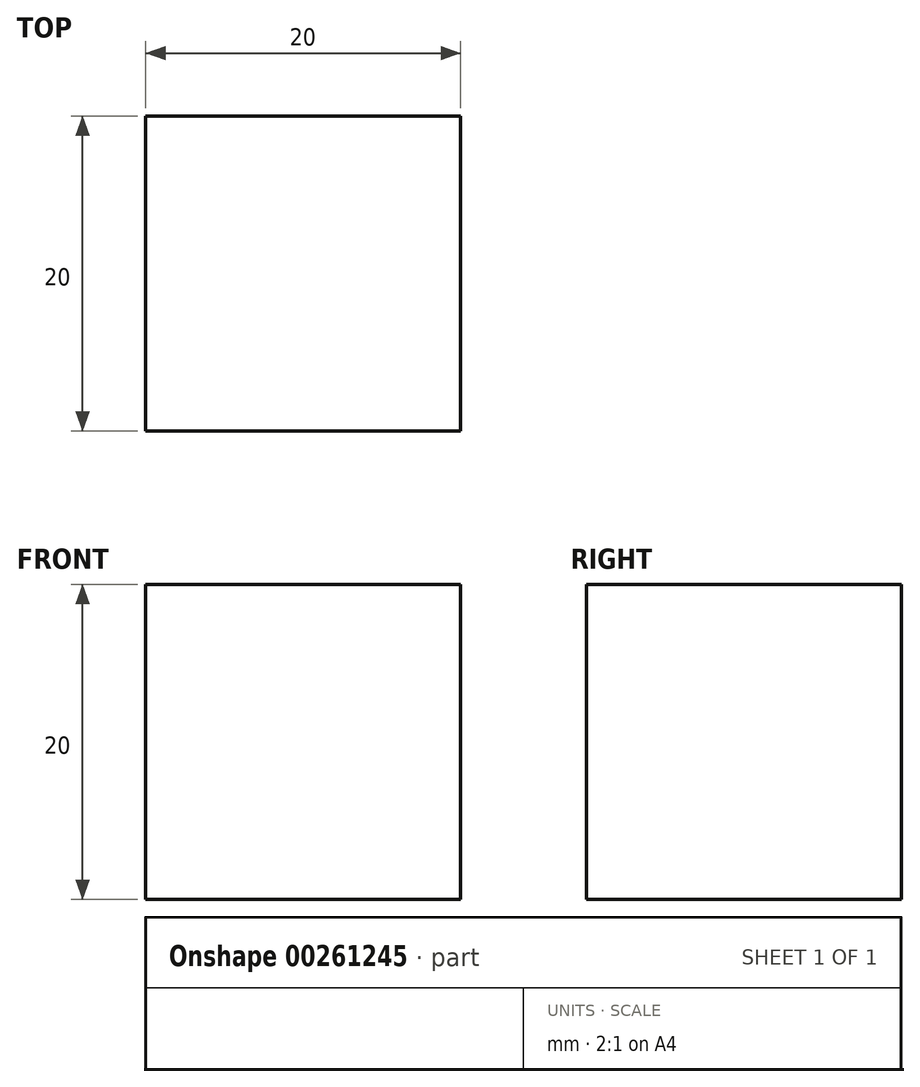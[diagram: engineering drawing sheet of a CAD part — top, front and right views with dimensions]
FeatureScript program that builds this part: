
annotation { "Feature Type Name" : "Feature", "Feature Type Description" : "" }
export const myFeature = defineFeature(function(context is Context, id is Id, definition is map)
    precondition{}
    {
        {
            var Q0;
            Q0=qCreatedBy(makeId("Top.planeOp"),FACE);
            var sketch = newSketch(context, id + "F0", { "sketchPlane" : qUnion([Q0])});
            skLineSegment(sketch, "E0.bottom", {"start": v(-10, 10) * mm, "end": v(10, 10) * mm});
            skLineSegment(sketch, "E0.top", {"start": v(-10, -10) * mm, "end": v(10, -10) * mm});
            skLineSegment(sketch, "E0.left", {"start": v(-10, 10) * mm, "end": v(-10, -10) * mm});
            skLineSegment(sketch, "E0.right", {"start": v(10, 10) * mm, "end": v(10, -10) * mm});
            skPoint(sketch, "E0.middle", {"position": v(0, 0) * mm});
            skSolve(sketch);
        }
        {
            var Q0;
            Q0 = qSketchRegion(id + "F0", true);
            extrude(context, id + "F1", {"entities" : qUnion([Q0]), "depth" : 20 * mm});
        }
    });
